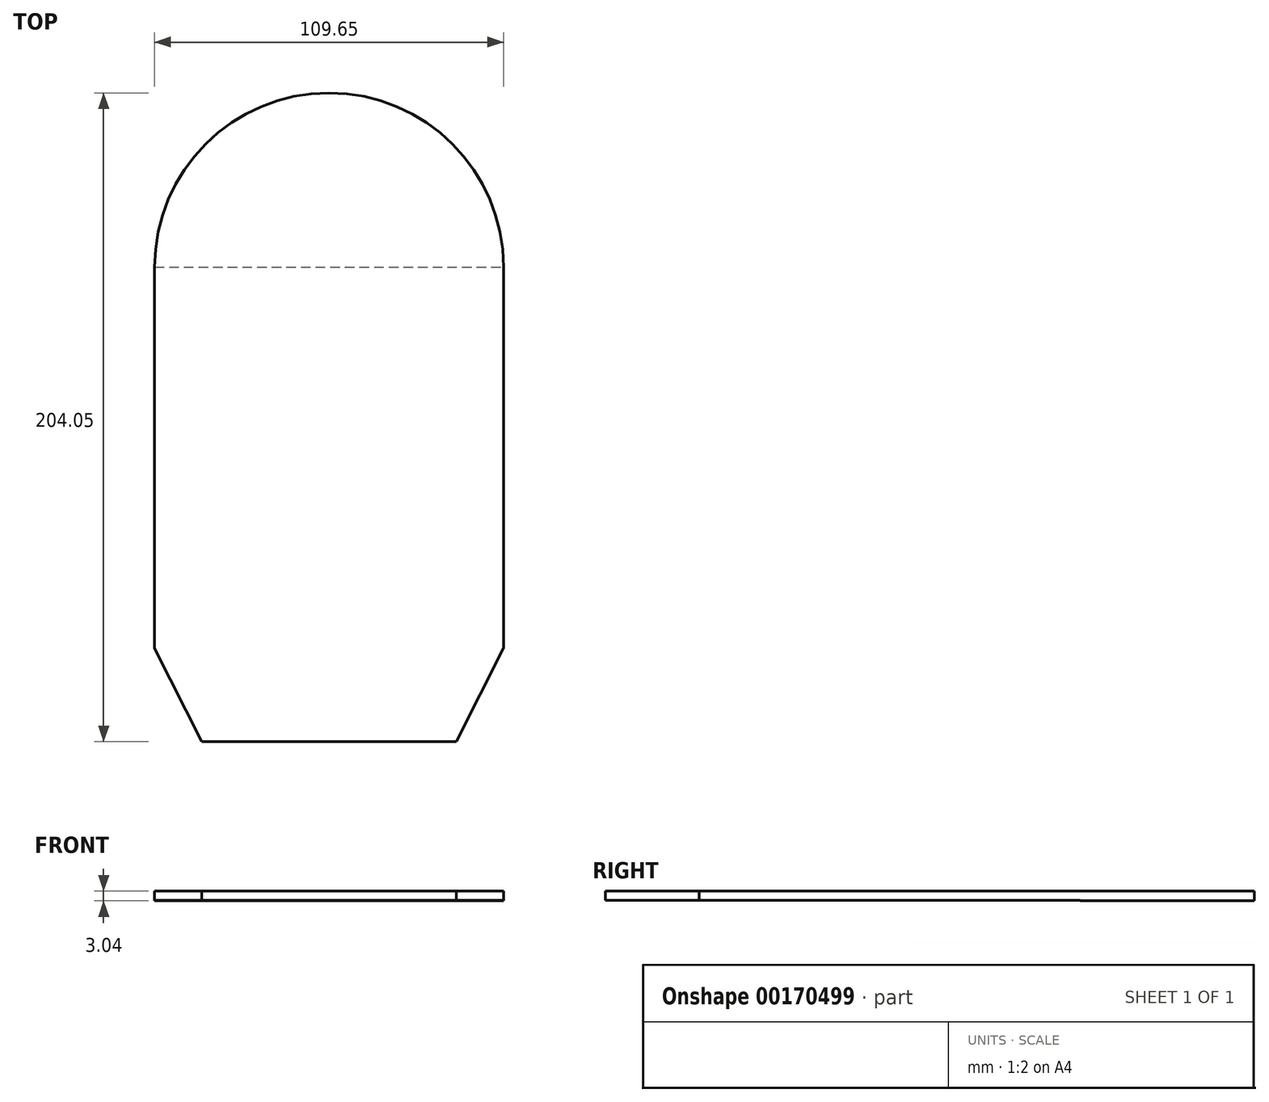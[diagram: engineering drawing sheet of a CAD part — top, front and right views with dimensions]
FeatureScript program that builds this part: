
annotation { "Feature Type Name" : "Feature", "Feature Type Description" : "" }
export const myFeature = defineFeature(function(context is Context, id is Id, definition is map)
    precondition{}
    {
        {
            var Q0;
            Q0=qCreatedBy(makeId("Top.planeOp"),FACE);
            var sketch = newSketch(context, id + "F0", { "sketchPlane" : qUnion([Q0])});
            skLineSegment(sketch, "E0.bottom", {"start": v(-41.56, 74.61) * mm, "end": v(68.1, 74.61) * mm});
            skLineSegment(sketch, "E0.top", {"start": v(-41.56, -74.61) * mm, "end": v(68.1, -74.61) * mm});
            skLineSegment(sketch, "E0.left", {"start": v(-41.56, 74.61) * mm, "end": v(-41.56, -74.61) * mm});
            skLineSegment(sketch, "E0.right", {"start": v(68.1, 74.61) * mm, "end": v(68.1, -74.61) * mm});
            skSolve(sketch);
        }
        {
            var Q0;
            Q0=makeQuery(id+"F0.imprint","IMPRINT",FACE,{"disambiguationData":[TD([[makeQuery(id+"F0.imprint","IMPRINT",EDGE,{"derivedFrom":sQuery(id+"F0.wireOp",EDGE,"E0.bottom")}),-1.0]])]});
            extrude(context, id + "F1", {"entities" : qUnion([Q0]), "depth" : 2.84 * mm});
        }
        {
            var Q0;
            Q0=makeQuery(id+"F1.opExtrude","CAP_FACE",FACE,{"disambiguationData":[OSD([sQuery(id+"F0.wireOp",EDGE,"E0.bottom"),sQuery(id+"F0.wireOp",EDGE,"E0.top"),sQuery(id+"F0.wireOp",EDGE,"E0.left"),sQuery(id+"F0.wireOp",EDGE,"E0.right")])],"isStart":false});
            var sketch = newSketch(context, id + "F2", { "sketchPlane" : qUnion([Q0])});
            skLineSegment(sketch, "E1", {"start": v(27.79, -74.61) * mm, "end": v(68.1, -75.24) * mm});
            skLineSegment(sketch, "E2", {"start": v(-25.02, -74.61) * mm, "end": v(-41.56, -75.71) * mm});
            skLineSegment(sketch, "E3", {"start": v(68.1, -74.61) * mm, "end": v(68.1, -75.24) * mm});
            skLineSegment(sketch, "E4", {"start": v(68.1, -74.61) * mm, "end": v(27.79, -74.61) * mm});
            skLineSegment(sketch, "E5", {"start": v(-25.02, -74.61) * mm, "end": v(-41.56, -74.61) * mm});
            skLineSegment(sketch, "E6", {"start": v(-41.56, -75.71) * mm, "end": v(-41.56, -74.61) * mm});
            skSolve(sketch);
        }
        {
            var Q0;
            Q0 = qSketchRegion(id + "F2", true);
            extrude(context, id + "F3", {"entities" : qUnion([Q0]), "operationType" : NewBodyOperationType.REMOVE, "oppositeDirection" : true, "depth" : 25.4 * mm});
        }
        {
            var Q0;
            Q0=makeQuery(id+"F1.opExtrude","CAP_FACE",FACE,{"disambiguationData":[OSD([sQuery(id+"F0.wireOp",EDGE,"E0.bottom"),sQuery(id+"F0.wireOp",EDGE,"E0.top"),sQuery(id+"F0.wireOp",EDGE,"E0.left"),sQuery(id+"F0.wireOp",EDGE,"E0.right")])],"isStart":false});
            var sketch = newSketch(context, id + "F4", { "sketchPlane" : qUnion([Q0])});
            skArc(sketch, "E7", {"start": v(68.1, 74.61) * mm, "mid": v(13.26, 129.44) * mm, "end": v(-41.56, 74.61) * mm});
            skSolve(sketch);
        }
        {
            var Q0;
            Q0=makeQuery(id+"F4.imprint","IMPRINT",FACE,{"disambiguationData":[TD([[makeQuery(id+"F4.imprint","IMPRINT",EDGE,{"derivedFrom":sQuery(id+"F4.wireOp",EDGE,"E7")}),1.0]])]});
            extrude(context, id + "F5", {"entities" : qUnion([Q0]), "operationType" : NewBodyOperationType.ADD, "oppositeDirection" : true, "depth" : 3.05 * mm});
        }
        {
            var Q0;
            Q0=makeQuery(id+"F1.opExtrude","SWEPT_BODY",BODY,{"disambiguationData":[OSD([sQuery(id+"F0.wireOp",EDGE,"E0.bottom"),sQuery(id+"F0.wireOp",EDGE,"E0.top"),sQuery(id+"F0.wireOp",EDGE,"E0.left"),sQuery(id+"F0.wireOp",EDGE,"E0.right")])]});
            transform(context, id + "F6", {"entities" : qUnion([Q0]), "transformType" : TransformType.TRANSLATION_3D, "dx" : -10.67 * mm, "dy" : 0 * mm, "dz" : 0 * mm, "makeCopy" : false});
        }
        {
            var Q0;
            Q0=makeQuery(id+"F1.opExtrude","SWEPT_BODY",BODY,{"disambiguationData":[OSD([sQuery(id+"F0.wireOp",EDGE,"E0.bottom"),sQuery(id+"F0.wireOp",EDGE,"E0.top"),sQuery(id+"F0.wireOp",EDGE,"E0.left"),sQuery(id+"F0.wireOp",EDGE,"E0.right")])]});
            transform(context, id + "F7", {"entities" : qUnion([Q0]), "transformType" : TransformType.TRANSLATION_3D, "dx" : -2.8 * mm, "dy" : 0 * mm, "dz" : 0 * mm, "makeCopy" : false});
        }
        {
            var Q0;
            Q0=qCreatedBy(makeId("Top.planeOp"),FACE);
            var sketch = newSketch(context, id + "F8", { "sketchPlane" : qUnion([Q0])});
            skLineSegment(sketch, "E8", {"start": v(-55.1, -74.79) * mm, "end": v(-40.16, -74.79) * mm});
            skLineSegment(sketch, "E9", {"start": v(-55.1, -74.79) * mm, "end": v(-55.1, -45.07) * mm});
            skLineSegment(sketch, "E10", {"start": v(-40.16, -74.79) * mm, "end": v(-55.1, -45.07) * mm});
            skLineSegment(sketch, "E11.MirrorCS", {"start": v(39.73, -74.72) * mm, "end": v(54.68, -45) * mm});
            skLineSegment(sketch, "E12.MirrorCS", {"start": v(54.68, -74.72) * mm, "end": v(39.73, -74.72) * mm});
            skLineSegment(sketch, "E13.MirrorCS", {"start": v(54.68, -74.72) * mm, "end": v(54.68, -45) * mm});
            skSolve(sketch);
        }
        {
            var Q0;
            Q0 = qSketchRegion(id + "F8", true);
            var Q1;
            Q1 = qSketchRegion(id + "FvXK6aXuZe8XkwM_1", true);
            extrude(context, id + "F9", {"entities" : qUnion([Q0, Q1]), "operationType" : NewBodyOperationType.REMOVE, "depth" : 107.44 * mm});
        }
    });
